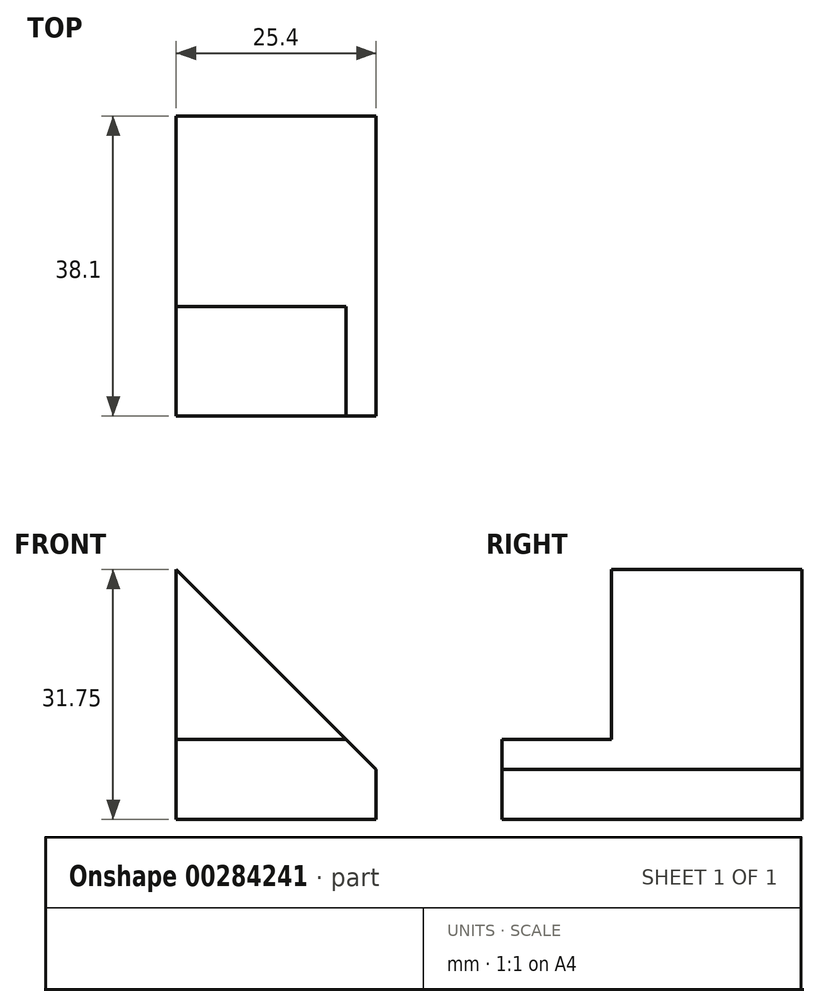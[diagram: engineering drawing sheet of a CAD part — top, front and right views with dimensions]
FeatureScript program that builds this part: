
annotation { "Feature Type Name" : "Feature", "Feature Type Description" : "" }
export const myFeature = defineFeature(function(context is Context, id is Id, definition is map)
    precondition{}
    {
        {
            var Q0;
            Q0=qCreatedBy(makeId("Front.planeOp"),FACE);
            var sketch = newSketch(context, id + "F0", { "sketchPlane" : qUnion([Q0])});
            skLineSegment(sketch, "E0", {"start": v(0, 0) * mm, "end": v(25.4, 0) * mm});
            skLineSegment(sketch, "E1", {"start": v(25.4, 0) * mm, "end": v(25.4, 6.35) * mm});
            skLineSegment(sketch, "E2", {"start": v(25.4, 6.35) * mm, "end": v(0, 6.35) * mm});
            skLineSegment(sketch, "E3", {"start": v(0, 6.35) * mm, "end": v(0, 0) * mm});
            skLineSegment(sketch, "E4", {"start": v(0, 6.35) * mm, "end": v(0, 31.75) * mm});
            skLineSegment(sketch, "E5", {"start": v(0, 31.75) * mm, "end": v(25.4, 6.35) * mm});
            skLineSegment(sketch, "E6", {"start": v(0, 25.4) * mm, "end": v(6.35, 25.4) * mm});
            skLineSegment(sketch, "E7", {"start": v(19.05, 12.7) * mm, "end": v(19.05, 6.35) * mm});
            skSolve(sketch);
        }
        {
            var Q0;
            Q0 = qSketchRegion(id + "F0", true);
            extrude(context, id + "F1", {"entities" : qUnion([Q0]), "depth" : 38.1 * mm});
        }
        {
            var Q0;
            Q0=makeQuery(id+"F1.opExtrude","SWEPT_FACE",FACE,{"disambiguationData":[OSD([sQuery(id+"F0.wireOp",EDGE,"E3"),sQuery(id+"F0.wireOp",EDGE,"E4")])]});
            var sketch = newSketch(context, id + "F2", { "sketchPlane" : qUnion([Q0])});
            skLineSegment(sketch, "E8", {"start": v(8.06, 31.75) * mm, "end": v(8.06, 23.48) * mm});
            skLineSegment(sketch, "E9", {"start": v(8.06, 23.48) * mm, "end": v(24.18, 23.48) * mm});
            skLineSegment(sketch, "E10", {"start": v(24.18, 23.48) * mm, "end": v(24.18, 15.82) * mm});
            skLineSegment(sketch, "E11", {"start": v(24.18, 15.82) * mm, "end": v(8.06, 15.82) * mm});
            skLineSegment(sketch, "E12", {"start": v(8.06, 15.82) * mm, "end": v(8.06, 6.35) * mm});
            skLineSegment(sketch, "E13", {"start": v(24.18, 31.75) * mm, "end": v(24.18, 23.48) * mm});
            skLineSegment(sketch, "E14", {"start": v(24.18, 15.82) * mm, "end": v(24.18, 10.18) * mm});
            skLineSegment(sketch, "E15", {"start": v(24.18, 10.18) * mm, "end": v(38.1, 10.18) * mm});
            skSolve(sketch);
        }
        {
            var Q0;
            Q0 = qSketchRegion(id + "F2", true);
            var Q1;
            Q1=makeQuery(id+"F2.imprint","IMPRINT",FACE,{"disambiguationData":[TD([[makeQuery(id+"F2.imprint","IMPRINT",EDGE,{"derivedFrom":sQuery(id+"F2.wireOp",EDGE,"E10")}),1.0]])]});
            extrude(context, id + "F3", {"entities" : qUnion([Q0, Q1]), "operationType" : NewBodyOperationType.REMOVE, "oppositeDirection" : true, "depth" : 25.4 * mm});
        }
    });
